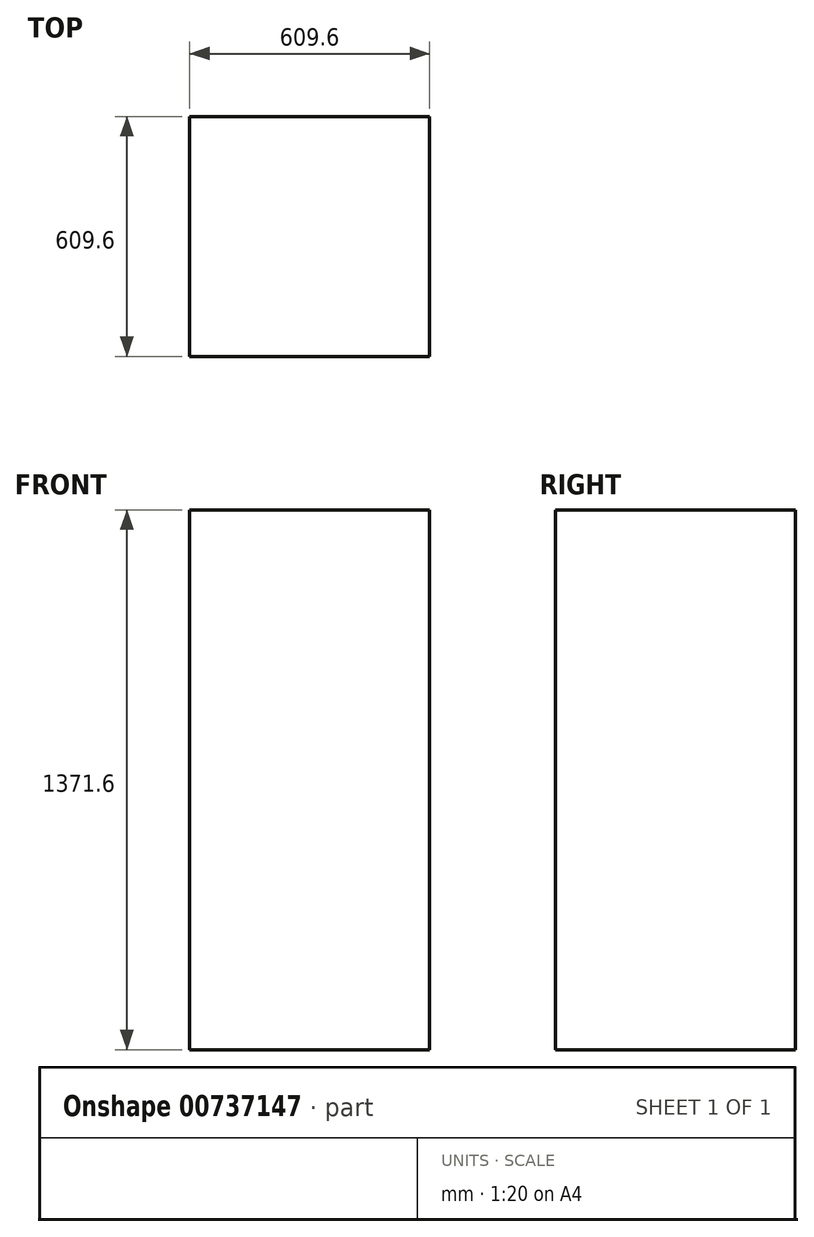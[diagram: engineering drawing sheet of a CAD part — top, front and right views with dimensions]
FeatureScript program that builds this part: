
annotation { "Feature Type Name" : "Feature", "Feature Type Description" : "" }
export const myFeature = defineFeature(function(context is Context, id is Id, definition is map)
    precondition{}
    {
        {
            var Q0;
            Q0=qCreatedBy(makeId("Front.planeOp"),FACE);
            var sketch = newSketch(context, id + "F0", { "sketchPlane" : qUnion([Q0])});
            skLineSegment(sketch, "E0.bottom", {"start": v(-302.28, 875.26) * mm, "end": v(307.32, 875.26) * mm});
            skLineSegment(sketch, "E0.top", {"start": v(-302.28, -496.34) * mm, "end": v(307.32, -496.34) * mm});
            skLineSegment(sketch, "E0.left", {"start": v(-302.28, 875.26) * mm, "end": v(-302.28, -496.34) * mm});
            skLineSegment(sketch, "E0.right", {"start": v(307.32, 875.26) * mm, "end": v(307.32, -496.34) * mm});
            skSolve(sketch);
        }
        {
            var Q0;
            Q0 = qSketchRegion(id + "F0", true);
            extrude(context, id + "F1", {"entities" : qUnion([Q0]), "depth" : 609.6 * mm, "offsetDistance" : 25.4 * mm});
        }
    });
